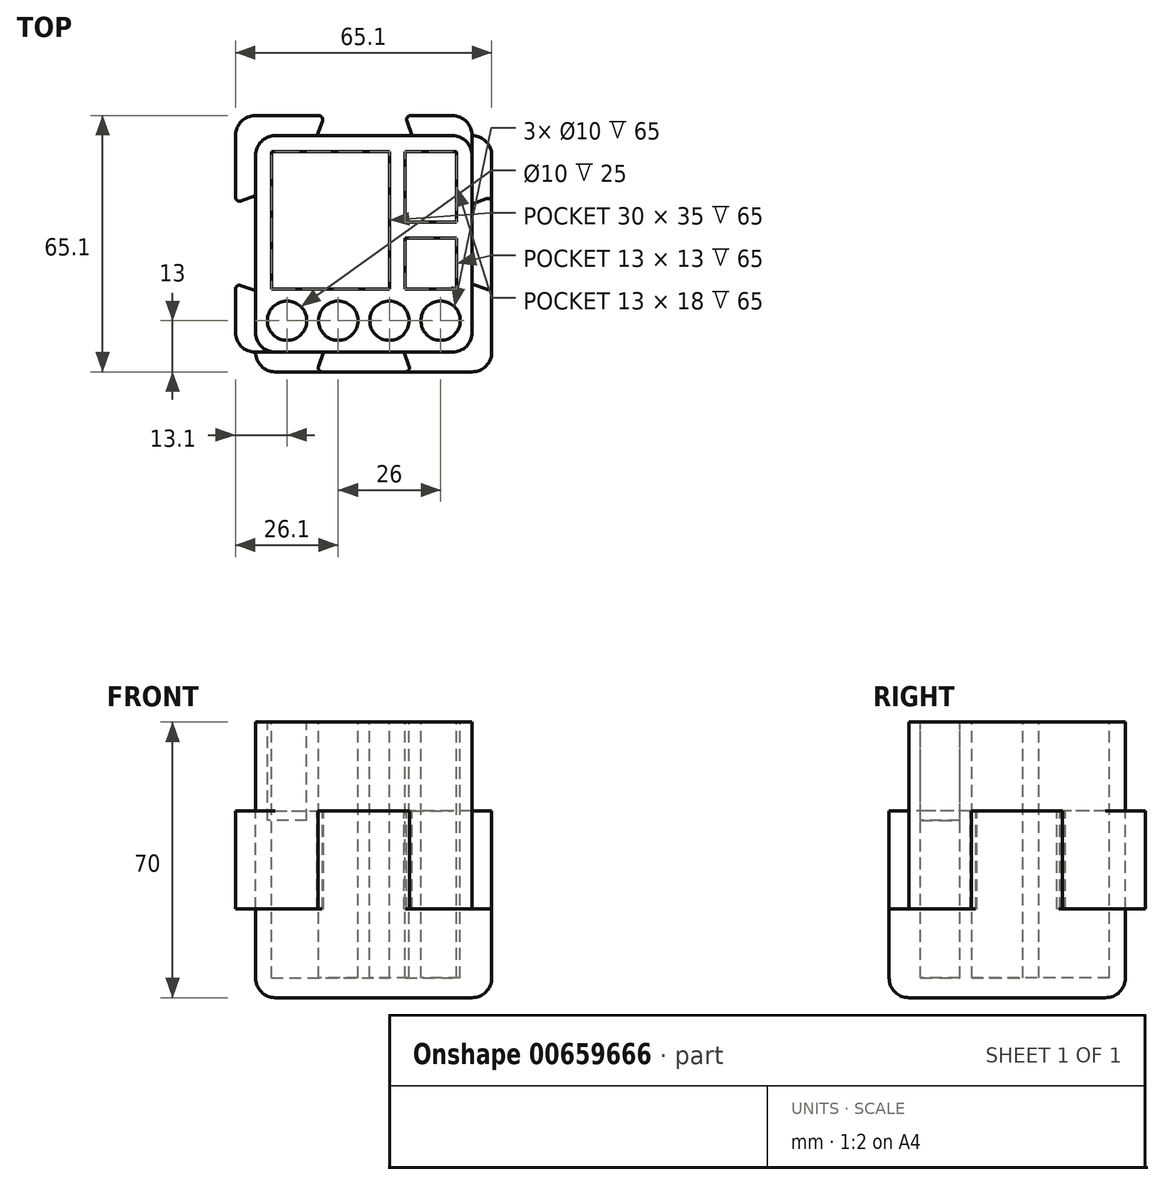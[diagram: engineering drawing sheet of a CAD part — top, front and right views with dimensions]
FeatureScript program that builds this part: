
annotation { "Feature Type Name" : "Feature", "Feature Type Description" : "" }
export const myFeature = defineFeature(function(context is Context, id is Id, definition is map)
    precondition{}
    {
        {
            var Q0;
            Q0=qCreatedBy(makeId("Top.planeOp"),FACE);
            var sketch = newSketch(context, id + "F0", { "sketchPlane" : qUnion([Q0])});
            skLineSegment(sketch, "E0.bottom", {"start": v(-27.5, 27.5) * mm, "end": v(27.5, 27.5) * mm});
            skLineSegment(sketch, "E0.top", {"start": v(-27.5, -27.5) * mm, "end": v(27.5, -27.5) * mm});
            skLineSegment(sketch, "E0.left", {"start": v(-27.5, 27.5) * mm, "end": v(-27.5, -27.5) * mm});
            skLineSegment(sketch, "E0.right", {"start": v(27.5, 27.5) * mm, "end": v(27.5, -27.5) * mm});
            skPoint(sketch, "E0.middle", {"position": v(0, 0) * mm});
            skLineSegment(sketch, "E1", {"start": v(-27.5, 27.5) * mm, "end": v(-32.6, 27.5) * mm});
            skLineSegment(sketch, "E2", {"start": v(-32.6, 27.5) * mm, "end": v(-32.6, 10.44) * mm});
            skLineSegment(sketch, "E3", {"start": v(-32.6, 10.44) * mm, "end": v(-27.5, 12.3) * mm});
            skLineSegment(sketch, "E4", {"start": v(-27.5, -11.9) * mm, "end": v(-32.6, -10.04) * mm});
            skLineSegment(sketch, "E5", {"start": v(-32.6, -10.04) * mm, "end": v(-32.6, -27.5) * mm});
            skLineSegment(sketch, "E6", {"start": v(-32.6, -27.5) * mm, "end": v(-27.5, -27.5) * mm});
            skLineSegment(sketch, "E7", {"start": v(-27.5, 27.5) * mm, "end": v(-27.5, 32.6) * mm});
            skLineSegment(sketch, "E8", {"start": v(-27.5, 32.6) * mm, "end": v(-10.04, 32.6) * mm});
            skLineSegment(sketch, "E9", {"start": v(-10.04, 32.6) * mm, "end": v(-11.9, 27.5) * mm});
            skLineSegment(sketch, "E10", {"start": v(27.5, 27.5) * mm, "end": v(27.5, 32.6) * mm});
            skLineSegment(sketch, "E11", {"start": v(27.5, 32.6) * mm, "end": v(10.44, 32.6) * mm});
            skLineSegment(sketch, "E12", {"start": v(10.44, 32.6) * mm, "end": v(12.3, 27.5) * mm});
            skLineSegment(sketch, "E13", {"start": v(-10.18, -27.5) * mm, "end": v(-12, -32.5) * mm});
            skLineSegment(sketch, "E14", {"start": v(-12, -32.5) * mm, "end": v(12, -32.5) * mm});
            skLineSegment(sketch, "E15", {"start": v(12, -32.5) * mm, "end": v(10.18, -27.5) * mm});
            skPoint(sketch, "E16", {"position": v(0, -32.5) * mm});
            skLineSegment(sketch, "E17", {"start": v(27.5, -10.18) * mm, "end": v(32.5, -12) * mm});
            skLineSegment(sketch, "E18", {"start": v(32.5, -12) * mm, "end": v(32.5, 12) * mm});
            skLineSegment(sketch, "E19", {"start": v(32.5, 12) * mm, "end": v(27.5, 10.18) * mm});
            skPoint(sketch, "E20", {"position": v(32.5, 0) * mm});
            skLineSegment(sketch, "E21", {"start": v(-32.6, 27.5) * mm, "end": v(-32.6, 32.6) * mm});
            skLineSegment(sketch, "E22", {"start": v(-32.6, 32.6) * mm, "end": v(-27.5, 32.6) * mm});
            skSolve(sketch);
        }
        {
            var Q0;
            {var subQ1=sQuery(id+"F0.wireOp",EDGE,"E0.bottom");Q0=makeQuery(id+"F0.imprint","IMPRINT",FACE,{"disambiguationData":[TD([[makeQuery(id+"F0.imprint","IMPRINT",EDGE,{"derivedFrom":subQ1}),-1.0]])]});}
            extrude(context, id + "F1", {"entities" : qUnion([Q0]), "oppositeDirection" : true, "depth" : 70 * mm, "offsetDistance" : 25 * mm, "symmetric" : true});
        }
        {
            var Q0;
            {var subQ0=sQuery(id+"F0.wireOp",EDGE,"E1");Q0=makeQuery(id+"F0.imprint","IMPRINT",FACE,{"disambiguationData":[TD([[makeQuery(id+"F0.imprint","IMPRINT",EDGE,{"derivedFrom":subQ0}),1.0]])]});}
            var Q1;
            {var subQ2=sQuery(id+"F0.wireOp",EDGE,"E4");Q1=makeQuery(id+"F0.imprint","IMPRINT",FACE,{"disambiguationData":[TD([[makeQuery(id+"F0.imprint","IMPRINT",EDGE,{"derivedFrom":subQ2}),1.0]])]});}
            var Q2;
            {var subQ2=sQuery(id+"F0.wireOp",EDGE,"E7");Q2=makeQuery(id+"F0.imprint","IMPRINT",FACE,{"disambiguationData":[TD([[makeQuery(id+"F0.imprint","IMPRINT",EDGE,{"derivedFrom":subQ2}),-1.0]])]});}
            var Q3;
            {var subQ0=sQuery(id+"F0.wireOp",EDGE,"E10");Q3=makeQuery(id+"F0.imprint","IMPRINT",FACE,{"disambiguationData":[TD([[makeQuery(id+"F0.imprint","IMPRINT",EDGE,{"derivedFrom":subQ0}),1.0]])]});}
            var Q4;
            {var subQ2=sQuery(id+"F0.wireOp",EDGE,"E13");Q4=makeQuery(id+"F0.imprint","IMPRINT",FACE,{"disambiguationData":[TD([[makeQuery(id+"F0.imprint","IMPRINT",EDGE,{"derivedFrom":subQ2}),1.0]])]});}
            var Q5;
            {var subQ0=sQuery(id+"F0.wireOp",EDGE,"E17");Q5=makeQuery(id+"F0.imprint","IMPRINT",FACE,{"disambiguationData":[TD([[makeQuery(id+"F0.imprint","IMPRINT",EDGE,{"derivedFrom":subQ0}),1.0]])]});}
            var Q6;
            Q6=makeQuery(id+"F0.imprint","IMPRINT",FACE,{"disambiguationData":[TD([[makeQuery(id+"F0.imprint","IMPRINT",EDGE,{"derivedFrom":sQuery(id+"F0.wireOp",EDGE,"E1")}),-1.0]])]});
            extrude(context, id + "F2", {"entities" : qUnion([Q0, Q1, Q2, Q3, Q4, Q5, Q6]), "operationType" : NewBodyOperationType.ADD, "oppositeDirection" : true, "depth" : 25 * mm, "offsetDistance" : 25 * mm, "symmetric" : true});
        }
        {
            var Q0;
            Q0=makeQuery(id+"F1.opExtrude","CAP_FACE",FACE,{"disambiguationData":[OSD([sQuery(id+"F0.wireOp",EDGE,"E0.bottom"),sQuery(id+"F0.wireOp",EDGE,"E0.top"),sQuery(id+"F0.wireOp",EDGE,"E0.left"),sQuery(id+"F0.wireOp",EDGE,"E0.right")])],"isStart":false});
            var sketch = newSketch(context, id + "F3", { "sketchPlane" : qUnion([Q0])});
            skLineSegment(sketch, "E23", {"start": v(-27.5, 27.5) * mm, "end": v(-27.5, 32.5) * mm});
            skLineSegment(sketch, "E24", {"start": v(-27.5, 32.5) * mm, "end": v(32.5, 32.5) * mm});
            skLineSegment(sketch, "E25", {"start": v(32.5, 32.5) * mm, "end": v(32.5, -27.5) * mm});
            skLineSegment(sketch, "E26", {"start": v(32.5, -27.5) * mm, "end": v(27.5, -27.5) * mm});
            skLineSegment(sketch, "E27", {"start": v(27.5, -27.5) * mm, "end": v(27.5, 27.5) * mm});
            skLineSegment(sketch, "E28", {"start": v(27.5, 27.5) * mm, "end": v(-27.5, 27.5) * mm});
            skSolve(sketch);
        }
        {
            var Q0;
            Q0 = qSketchRegion(id + "F3", true);
            var Q1;
            Q1=makeQuery(id+"F2.opExtrude","CAP_FACE",FACE,{"disambiguationData":[OSD([sQuery(id+"F0.wireOp",EDGE,"E0.right"),sQuery(id+"F0.wireOp",EDGE,"E17"),sQuery(id+"F0.wireOp",EDGE,"E18"),sQuery(id+"F0.wireOp",EDGE,"E19")])],"isStart":false});
            extrude(context, id + "F4", {"entities" : qUnion([Q0]), "operationType" : NewBodyOperationType.ADD, "endBound" : BoundingType.UP_TO_SURFACE, "oppositeDirection" : true, "depth" : 25 * mm, "endBoundEntityFace" : qUnion([Q1]), "offsetDistance" : 25 * mm});
        }
        {
            var Q0;
            Q0=makeQuery(id+"F2.opExtrude","SWEPT_EDGE",EDGE,{"disambiguationData":[OSD([sQuery(id+"F0.wireOp",EDGE,"E21"),sQuery(id+"F0.wireOp",EDGE,"E22")])]});
            var Q1;
            {var subQ0=sQuery(id+"F0.wireOp",EDGE,"E0.bottom");var subQ1=sQuery(id+"F0.wireOp",EDGE,"E0.left");Q1=makeQuery(id+"F2.boolean.opBoolean","SPLIT",EDGE,{"disambiguationData":[TD([makeQuery(id+"F1.opExtrude","CAP_FACE",FACE,{"disambiguationData":[OSD([subQ0,sQuery(id+"F0.wireOp",EDGE,"E0.top"),subQ1,sQuery(id+"F0.wireOp",EDGE,"E0.right")])],"isStart":true})])],"derivedFrom":makeQuery(id+"F1.opExtrude","SWEPT_EDGE",EDGE,{"disambiguationData":[OSD([subQ0,subQ1,sQuery(id+"F0.wireOp",EDGE,"E1"),sQuery(id+"F0.wireOp",EDGE,"E7")])]})});}
            var Q2;
            {var subQ0=sQuery(id+"F0.wireOp",EDGE,"E0.bottom");var subQ1=sQuery(id+"F0.wireOp",EDGE,"E0.left");Q2=makeQuery(id+"F2.boolean.opBoolean","SPLIT",EDGE,{"disambiguationData":[TD([makeQuery(id+"F1.opExtrude","CAP_FACE",FACE,{"disambiguationData":[OSD([subQ0,sQuery(id+"F0.wireOp",EDGE,"E0.top"),subQ1,sQuery(id+"F0.wireOp",EDGE,"E0.right")])],"isStart":false})])],"derivedFrom":makeQuery(id+"F1.opExtrude","SWEPT_EDGE",EDGE,{"disambiguationData":[OSD([subQ0,subQ1,sQuery(id+"F0.wireOp",EDGE,"E1"),sQuery(id+"F0.wireOp",EDGE,"E7")])]})});}
            var Q3;
            Q3=makeQuery(id+"F2.opExtrude","SWEPT_EDGE",EDGE,{"disambiguationData":[OSD([sQuery(id+"F0.wireOp",EDGE,"E5"),sQuery(id+"F0.wireOp",EDGE,"E6")])]});
            var Q4;
            Q4=makeQuery(id+"F4.opExtrude","SWEPT_EDGE",EDGE,{"disambiguationData":[OSD([sQuery(id+"F3.wireOp",EDGE,"E23"),sQuery(id+"F3.wireOp",EDGE,"E24")])]});
            var Q5;
            Q5=makeQuery(id+"F4.opExtrude","SWEPT_EDGE",EDGE,{"disambiguationData":[OSD([sQuery(id+"F3.wireOp",EDGE,"E24"),sQuery(id+"F3.wireOp",EDGE,"E25")])]});
            var Q6;
            Q6=makeQuery(id+"F1.opExtrude","SWEPT_EDGE",EDGE,{"disambiguationData":[OSD([sQuery(id+"F0.wireOp",EDGE,"E0.top"),sQuery(id+"F0.wireOp",EDGE,"E0.right")])]});
            var Q7;
            Q7=makeQuery(id+"F4.opExtrude","SWEPT_EDGE",EDGE,{"disambiguationData":[OSD([sQuery(id+"F3.wireOp",EDGE,"E25"),sQuery(id+"F3.wireOp",EDGE,"E26")])]});
            var Q8;
            Q8=makeQuery(id+"F2.opExtrude","SWEPT_EDGE",EDGE,{"disambiguationData":[OSD([sQuery(id+"F0.wireOp",EDGE,"E10"),sQuery(id+"F0.wireOp",EDGE,"E11")])]});
            var Q9;
            {var subQ0=sQuery(id+"F0.wireOp",EDGE,"E0.right");var subQ1=sQuery(id+"F0.wireOp",EDGE,"E0.bottom");var subQ2=sQuery(id+"F0.wireOp",EDGE,"E10");Q9=makeQuery(id+"F2.boolean.opBoolean","SPLIT",EDGE,{"disambiguationData":[TD([makeQuery(id+"F1.opExtrude","CAP_FACE",FACE,{"disambiguationData":[OSD([subQ1,sQuery(id+"F0.wireOp",EDGE,"E0.top"),sQuery(id+"F0.wireOp",EDGE,"E0.left"),subQ0])],"isStart":true})])],"derivedFrom":makeQuery(id+"F1.opExtrude","SWEPT_EDGE",EDGE,{"disambiguationData":[OSD([subQ1,subQ0,subQ2])]})});}
            var Q10;
            Q10=makeQuery(id+"F4.opExtrude","CAP_EDGE",EDGE,{"disambiguationData":[OSD([sQuery(id+"F3.wireOp",EDGE,"E25")])],"isStart":true});
            var Q11;
            Q11=makeQuery(id+"F4.opExtrude","CAP_EDGE",EDGE,{"disambiguationData":[OSD([sQuery(id+"F3.wireOp",EDGE,"E24")])],"isStart":true});
            var Q12;
            Q12=makeQuery(id+"F4.boolean.opBoolean","MERGE",EDGE,{"derivedFrom":[makeQuery(id+"F1.opExtrude","CAP_EDGE",EDGE,{"disambiguationData":[OSD([sQuery(id+"F0.wireOp",EDGE,"E0.left")])],"isStart":false}),makeQuery(id+"F4.opExtrude","CAP_EDGE",EDGE,{"disambiguationData":[OSD([sQuery(id+"F3.wireOp",EDGE,"E23")])],"isStart":true})]});
            var Q13;
            Q13=makeQuery(id+"F4.boolean.opBoolean","MERGE",EDGE,{"derivedFrom":[makeQuery(id+"F1.opExtrude","CAP_EDGE",EDGE,{"disambiguationData":[OSD([sQuery(id+"F0.wireOp",EDGE,"E0.bottom")])],"isStart":false}),makeQuery(id+"F4.opExtrude","CAP_EDGE",EDGE,{"disambiguationData":[OSD([sQuery(id+"F3.wireOp",EDGE,"E26")])],"isStart":true})]});
            var Q14;
            {var subQ0=sQuery(id+"F0.wireOp",EDGE,"E0.left");var subQ1=sQuery(id+"F0.wireOp",EDGE,"E0.top");var subQ2=sQuery(id+"F0.wireOp",EDGE,"E6");Q14=makeQuery(id+"F2.boolean.opBoolean","SPLIT",EDGE,{"disambiguationData":[TD([makeQuery(id+"F1.opExtrude","CAP_FACE",FACE,{"disambiguationData":[OSD([sQuery(id+"F0.wireOp",EDGE,"E0.bottom"),subQ1,subQ0,sQuery(id+"F0.wireOp",EDGE,"E0.right")])],"isStart":true})])],"derivedFrom":makeQuery(id+"F1.opExtrude","SWEPT_EDGE",EDGE,{"disambiguationData":[OSD([subQ1,subQ0,subQ2])]})});}
            fillet(context, id + "F5", {"entities" : qUnion([Q0, Q1, Q2, Q3, Q4, Q5, Q6, Q7, Q8, Q9, Q10, Q11, Q12, Q13, Q14]), "tangentPropagation" : true, "radius" : 5 * mm, "defaultsChanged" : false, "vertexSettings" : [], "allowEdgeOverflow" : false});
        }
        {
            var Q0;
            Q0=makeQuery(id+"F2.opExtrude","SWEPT_EDGE",EDGE,{"disambiguationData":[OSD([sQuery(id+"F0.wireOp",EDGE,"E14"),sQuery(id+"F0.wireOp",EDGE,"E15")])]});
            var Q1;
            Q1=makeQuery(id+"F2.opExtrude","SWEPT_EDGE",EDGE,{"disambiguationData":[OSD([sQuery(id+"F0.wireOp",EDGE,"E13"),sQuery(id+"F0.wireOp",EDGE,"E14")])]});
            var Q2;
            Q2=makeQuery(id+"F2.opExtrude","SWEPT_EDGE",EDGE,{"disambiguationData":[OSD([sQuery(id+"F0.wireOp",EDGE,"E17"),sQuery(id+"F0.wireOp",EDGE,"E18")])]});
            var Q3;
            Q3=makeQuery(id+"F2.opExtrude","SWEPT_EDGE",EDGE,{"disambiguationData":[OSD([sQuery(id+"F0.wireOp",EDGE,"E18"),sQuery(id+"F0.wireOp",EDGE,"E19")])]});
            var Q4;
            Q4=makeQuery(id+"F2.opExtrude","SWEPT_EDGE",EDGE,{"disambiguationData":[OSD([sQuery(id+"F0.wireOp",EDGE,"E11"),sQuery(id+"F0.wireOp",EDGE,"E12")])]});
            var Q5;
            Q5=makeQuery(id+"F2.opExtrude","SWEPT_EDGE",EDGE,{"disambiguationData":[OSD([sQuery(id+"F0.wireOp",EDGE,"E8"),sQuery(id+"F0.wireOp",EDGE,"E9")])]});
            var Q6;
            Q6=makeQuery(id+"F2.opExtrude","SWEPT_EDGE",EDGE,{"disambiguationData":[OSD([sQuery(id+"F0.wireOp",EDGE,"E2"),sQuery(id+"F0.wireOp",EDGE,"E3")])]});
            var Q7;
            Q7=makeQuery(id+"F2.opExtrude","SWEPT_EDGE",EDGE,{"disambiguationData":[OSD([sQuery(id+"F0.wireOp",EDGE,"E4"),sQuery(id+"F0.wireOp",EDGE,"E5")])]});
            fillet(context, id + "F6", {"entities" : qUnion([Q0, Q1, Q2, Q3, Q4, Q5, Q6, Q7]), "tangentPropagation" : true, "radius" : 1 * mm, "defaultsChanged" : false, "vertexSettings" : [], "allowEdgeOverflow" : false});
        }
        {
            var Q0;
            Q0=makeQuery(id+"F1.opExtrude","CAP_FACE",FACE,{"disambiguationData":[OSD([sQuery(id+"F0.wireOp",EDGE,"E0.bottom"),sQuery(id+"F0.wireOp",EDGE,"E0.top"),sQuery(id+"F0.wireOp",EDGE,"E0.left"),sQuery(id+"F0.wireOp",EDGE,"E0.right")])],"isStart":true});
            var sketch = newSketch(context, id + "F7", { "sketchPlane" : qUnion([Q0])});
            skLineSegment(sketch, "E29.bottom", {"start": v(-23.5, 23.5) * mm, "end": v(6.5, 23.5) * mm});
            skLineSegment(sketch, "E29.top", {"start": v(-23.5, -11.5) * mm, "end": v(6.5, -11.5) * mm});
            skLineSegment(sketch, "E29.left", {"start": v(-23.5, 23.5) * mm, "end": v(-23.5, -11.5) * mm});
            skLineSegment(sketch, "E29.right", {"start": v(6.5, 23.5) * mm, "end": v(6.5, -11.5) * mm});
            skCircle(sketch, "E30", {"center": v(-6.5, -19.5) * mm, "radius": 5 * mm});
            skCircle(sketch, "E31", {"center": v(6.5, -19.5) * mm, "radius": 5 * mm});
            skCircle(sketch, "E32", {"center": v(-19.5, -19.5) * mm, "radius": 5 * mm});
            skCircle(sketch, "E33", {"center": v(19.5, -19.5) * mm, "radius": 5 * mm});
            skLineSegment(sketch, "E34", {"start": v(-6.5, -19.5) * mm, "end": v(6.5, -19.5) * mm, "construction": true});
            skPoint(sketch, "E35", {"position": v(0, -19.5) * mm});
            skLineSegment(sketch, "E36.bottom", {"start": v(10.5, 23.5) * mm, "end": v(23.5, 23.5) * mm});
            skLineSegment(sketch, "E36.top", {"start": v(10.5, 5.5) * mm, "end": v(23.5, 5.5) * mm});
            skLineSegment(sketch, "E36.left", {"start": v(10.5, 23.5) * mm, "end": v(10.5, 5.5) * mm});
            skLineSegment(sketch, "E36.right", {"start": v(23.5, 23.5) * mm, "end": v(23.5, 5.5) * mm});
            skLineSegment(sketch, "E37.bottom", {"start": v(10.5, -11.5) * mm, "end": v(23.5, -11.5) * mm});
            skLineSegment(sketch, "E37.top", {"start": v(10.5, 1.5) * mm, "end": v(23.5, 1.5) * mm});
            skLineSegment(sketch, "E37.left", {"start": v(10.5, -11.5) * mm, "end": v(10.5, 1.5) * mm});
            skLineSegment(sketch, "E37.right", {"start": v(23.5, -11.5) * mm, "end": v(23.5, 1.5) * mm});
            skSolve(sketch);
        }
        {
            var Q0;
            Q0=makeQuery(id+"F7.imprint","IMPRINT",FACE,{"disambiguationData":[TD([[makeQuery(id+"F7.imprint","IMPRINT",EDGE,{"derivedFrom":sQuery(id+"F7.wireOp",EDGE,"E29.bottom")}),-1.0]])]});
            var Q1;
            Q1=makeQuery(id+"F7.imprint","IMPRINT",FACE,{"disambiguationData":[TD([[makeQuery(id+"F7.imprint","IMPRINT",EDGE,{"derivedFrom":sQuery(id+"F7.wireOp",EDGE,"E30")}),1.0]])]});
            var Q2;
            Q2=makeQuery(id+"F7.imprint","IMPRINT",FACE,{"disambiguationData":[TD([[makeQuery(id+"F7.imprint","IMPRINT",EDGE,{"derivedFrom":sQuery(id+"F7.wireOp",EDGE,"E31")}),1.0]])]});
            var Q3;
            Q3=makeQuery(id+"F7.imprint","IMPRINT",FACE,{"disambiguationData":[TD([[makeQuery(id+"F7.imprint","IMPRINT",EDGE,{"derivedFrom":sQuery(id+"F7.wireOp",EDGE,"E36.bottom")}),-1.0]])]});
            var Q4;
            Q4=makeQuery(id+"F7.imprint","IMPRINT",FACE,{"disambiguationData":[TD([[makeQuery(id+"F7.imprint","IMPRINT",EDGE,{"derivedFrom":sQuery(id+"F7.wireOp",EDGE,"E37.bottom")}),1.0]])]});
            var Q5;
            Q5=makeQuery(id+"F7.imprint","IMPRINT",FACE,{"disambiguationData":[TD([[makeQuery(id+"F7.imprint","IMPRINT",EDGE,{"derivedFrom":sQuery(id+"F7.wireOp",EDGE,"E33")}),1.0]])]});
            extrude(context, id + "F8", {"entities" : qUnion([Q0, Q1, Q2, Q3, Q4, Q5]), "operationType" : NewBodyOperationType.REMOVE, "oppositeDirection" : true, "depth" : 65 * mm, "offsetDistance" : 25 * mm});
        }
        {
            var Q0;
            Q0=makeQuery(id+"F7.imprint","IMPRINT",FACE,{"disambiguationData":[TD([[makeQuery(id+"F7.imprint","IMPRINT",EDGE,{"derivedFrom":sQuery(id+"F7.wireOp",EDGE,"E32")}),1.0]])]});
            extrude(context, id + "F9", {"entities" : qUnion([Q0]), "operationType" : NewBodyOperationType.REMOVE, "oppositeDirection" : true, "depth" : 25 * mm, "offsetDistance" : 25 * mm});
        }
    });
